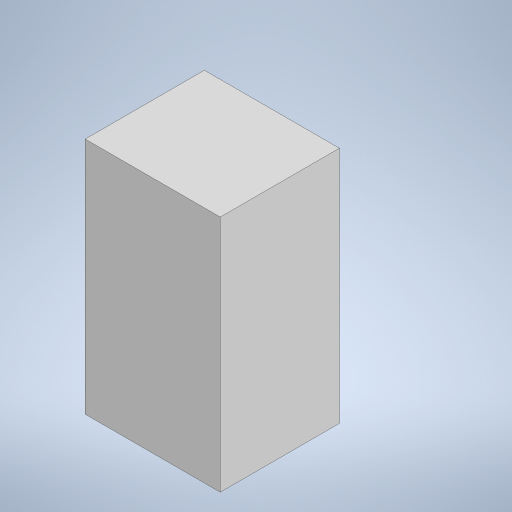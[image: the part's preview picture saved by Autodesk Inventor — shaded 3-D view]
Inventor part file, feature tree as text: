
AUTODESK INVENTOR PART (.ipt)
format: ipt  version: 2024.3 (Build 283343000, 343)  size: 195,072 bytes
history: native  units: mm
features: extrude x2, sketch x2, other x1
ambient origin geometry x8: Origin, YZ Plane, XZ Plane, XY Plane, X Axis, Y Axis, Z Axis, Center Point
bodies: Body1 (feature_tree)
feature tree (5):
  other  "ソリッド1"
  extrude  "押し出し1"  Depth=300.0mm
  extrude  "押し出し2"  Depth=170.0mm
  sketch  "スケッチ1"
  sketch  "スケッチ2"
